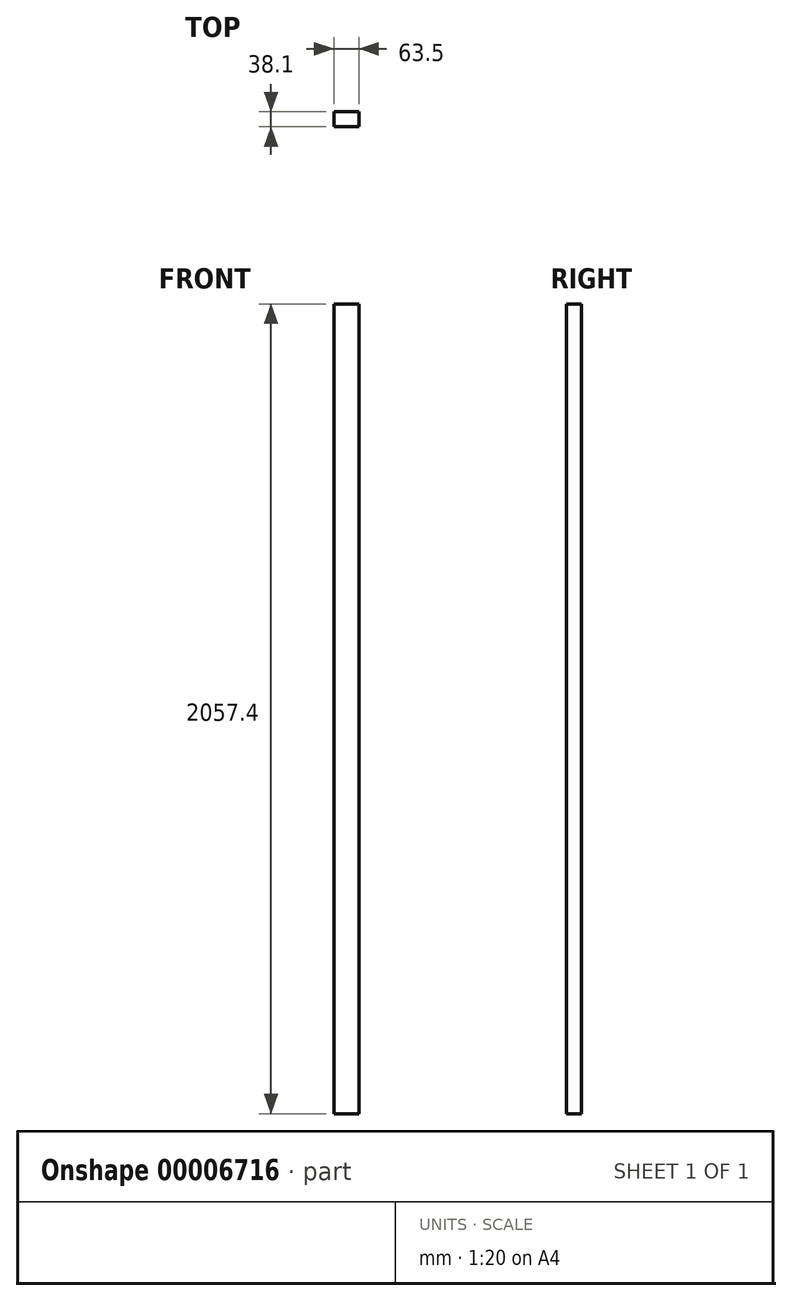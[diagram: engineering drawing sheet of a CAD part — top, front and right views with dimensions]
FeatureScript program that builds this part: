
annotation { "Feature Type Name" : "Feature", "Feature Type Description" : "" }
export const myFeature = defineFeature(function(context is Context, id is Id, definition is map)
    precondition{}
    {
        {
            var Q0;
            Q0=qCreatedBy(makeId("Top.planeOp"),FACE);
            var sketch = newSketch(context, id + "F0", { "sketchPlane" : qUnion([Q0])});
            skLineSegment(sketch, "E0.bottom", {"start": v(-19.05, 19.05) * mm, "end": v(44.45, 19.05) * mm});
            skLineSegment(sketch, "E0.top", {"start": v(-19.05, -19.05) * mm, "end": v(44.45, -19.05) * mm});
            skLineSegment(sketch, "E0.left", {"start": v(-19.05, 19.05) * mm, "end": v(-19.05, -19.05) * mm});
            skLineSegment(sketch, "E0.right", {"start": v(44.45, 19.05) * mm, "end": v(44.45, -19.05) * mm});
            skSolve(sketch);
        }
        {
            var Q0;
            Q0 = qSketchRegion(id + "F0", true);
            extrude(context, id + "F1", {"entities" : qUnion([Q0]), "depth" : 2057.4 * mm});
        }
    });
